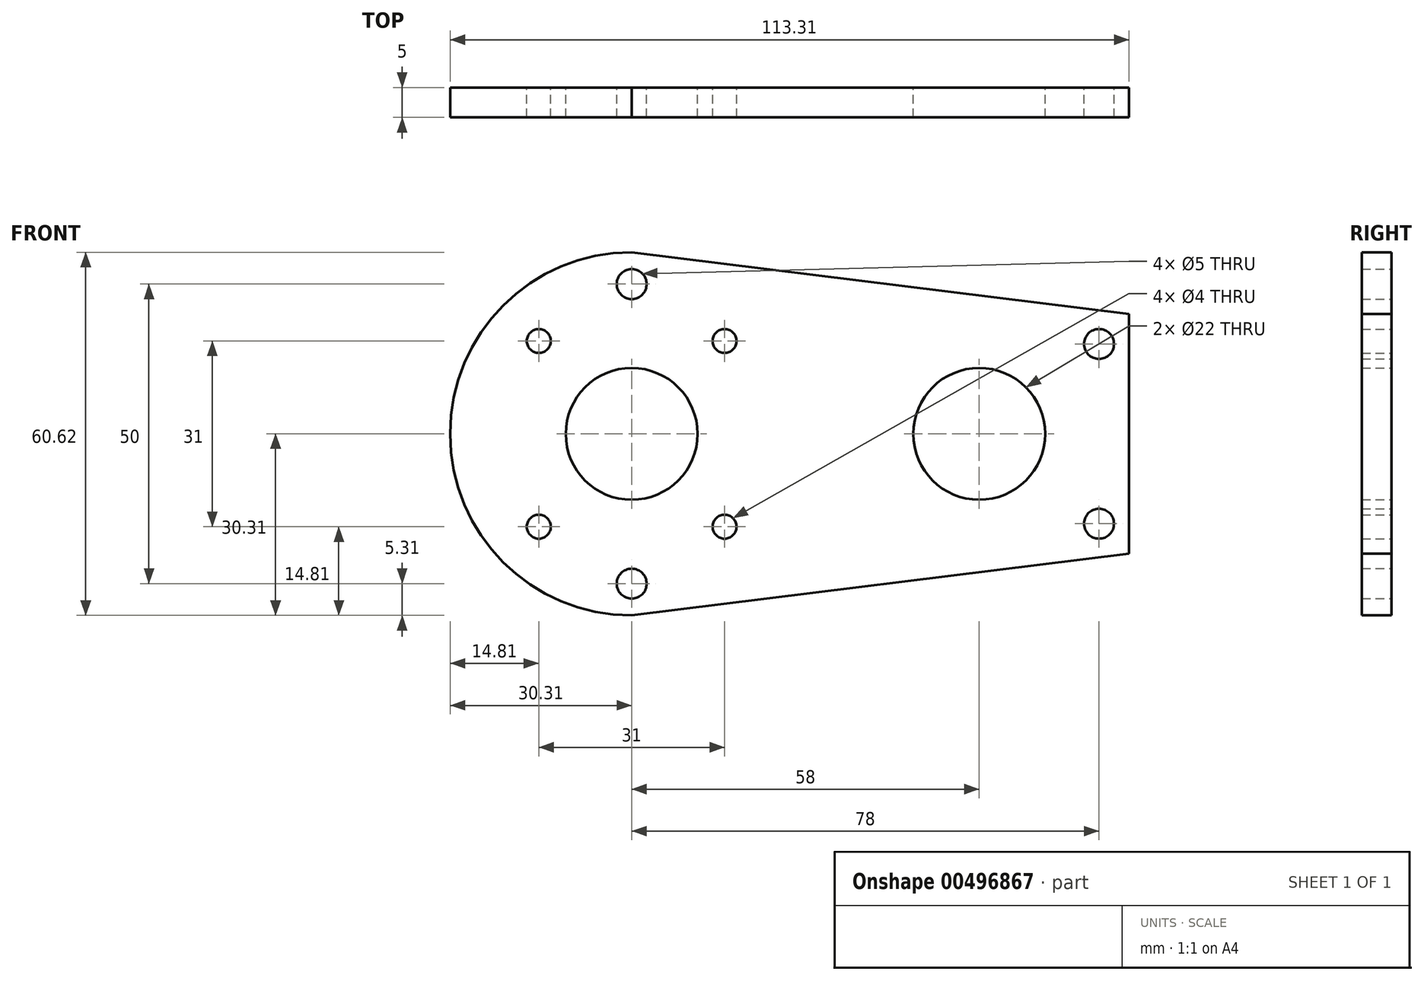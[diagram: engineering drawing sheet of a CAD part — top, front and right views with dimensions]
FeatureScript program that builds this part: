
annotation { "Feature Type Name" : "Feature", "Feature Type Description" : "" }
export const myFeature = defineFeature(function(context is Context, id is Id, definition is map)
    precondition{}
    {
        {
            var Q0;
            Q0=qCreatedBy(makeId("Front.planeOp"),FACE);
            var sketch = newSketch(context, id + "F0", { "sketchPlane" : qUnion([Q0])});
            skArc(sketch, "E0", {"start": v(0, -30.31) * mm, "mid": v(-30.31, 0) * mm, "end": v(0, 30.31) * mm});
            skCircle(sketch, "E1", {"center": v(0, 0) * mm, "radius": 11 * mm});
            skCircle(sketch, "E2", {"center": v(15.5, 15.5) * mm, "radius": 2 * mm});
            skCircle(sketch, "E3", {"center": v(-15.5, 15.5) * mm, "radius": 2 * mm});
            skCircle(sketch, "E4", {"center": v(-15.5, -15.5) * mm, "radius": 2 * mm});
            skCircle(sketch, "E5", {"center": v(15.5, -15.5) * mm, "radius": 2 * mm});
            skCircle(sketch, "E6", {"center": v(58, 0) * mm, "radius": 11 * mm});
            skLineSegment(sketch, "E7", {"start": v(58, 0) * mm, "end": v(83, 0) * mm});
            skLineSegment(sketch, "E8", {"start": v(83, 0) * mm, "end": v(83, 20) * mm});
            skLineSegment(sketch, "E9", {"start": v(83, 0) * mm, "end": v(83, -20) * mm});
            skLineSegment(sketch, "E10", {"start": v(0, -30.31) * mm, "end": v(83, -20) * mm});
            skLineSegment(sketch, "E11", {"start": v(0, 30.31) * mm, "end": v(83, 20) * mm});
            skCircle(sketch, "E12", {"center": v(0, 25) * mm, "radius": 2.5 * mm});
            skCircle(sketch, "E13", {"center": v(0, -25) * mm, "radius": 2.5 * mm});
            skCircle(sketch, "E14", {"center": v(78, -15) * mm, "radius": 2.5 * mm});
            skCircle(sketch, "E15", {"center": v(78, 15) * mm, "radius": 2.5 * mm});
            skSolve(sketch);
        }
        {
            var Q0;
            Q0 = qSketchRegion(id + "F0", true);
            extrude(context, id + "F1", {"entities" : qUnion([Q0]), "depth" : 5 * mm});
        }
    });
